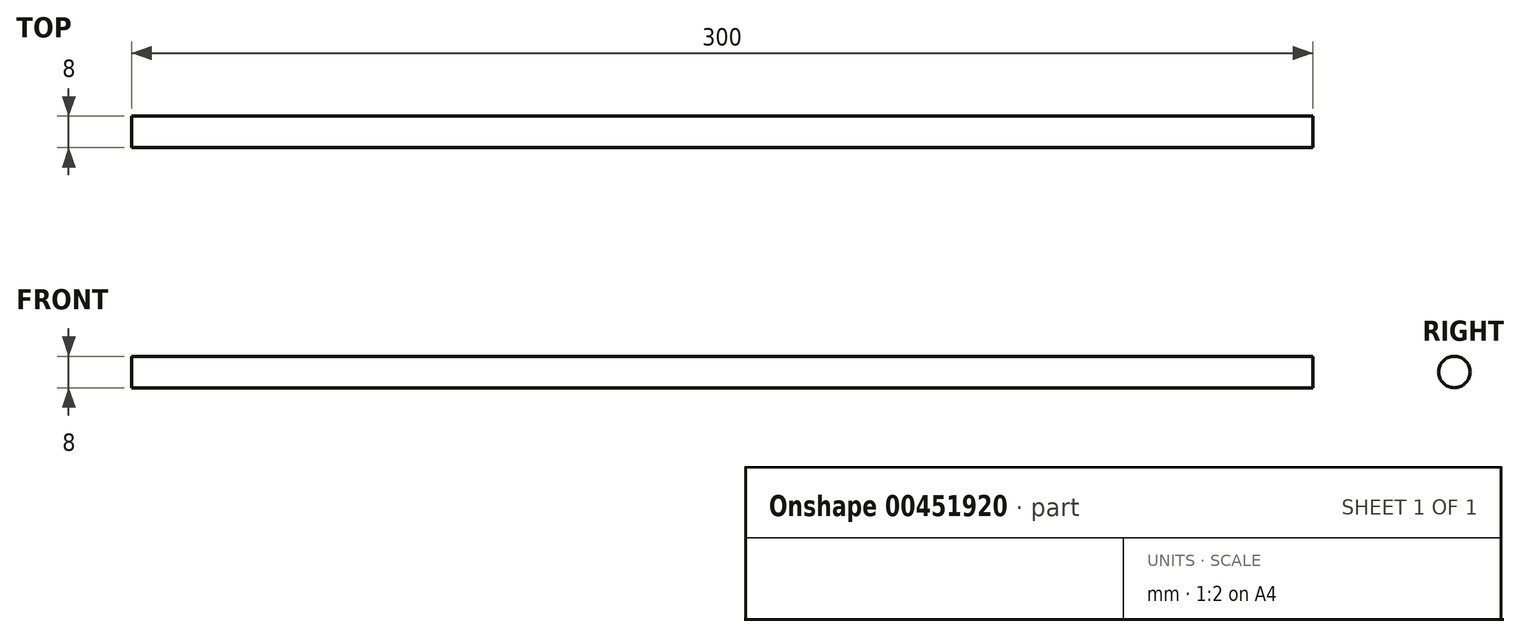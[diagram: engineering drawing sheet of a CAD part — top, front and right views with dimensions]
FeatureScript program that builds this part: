
annotation { "Feature Type Name" : "Feature", "Feature Type Description" : "" }
export const myFeature = defineFeature(function(context is Context, id is Id, definition is map)
    precondition{}
    {
        {
            var Q0;
            Q0=qCreatedBy(makeId("Top.planeOp"),FACE);
            var sketch = newSketch(context, id + "F0", { "sketchPlane" : qUnion([Q0])});
            skLineSegment(sketch, "E0", {"start": v(-150, 0) * mm, "end": v(-150, 4) * mm});
            skLineSegment(sketch, "E1", {"start": v(-150, 4) * mm, "end": v(-50, 4) * mm});
            skLineSegment(sketch, "E2", {"start": v(-50, 4) * mm, "end": v(-50, 4) * mm});
            skLineSegment(sketch, "E3", {"start": v(-50, 4) * mm, "end": v(0, 4) * mm});
            skLineSegment(sketch, "E4", {"start": v(0, -10.3) * mm, "end": v(0, 18.1) * mm, "construction": true});
            skLineSegment(sketch, "E5", {"start": v(-54.75, 0) * mm, "end": v(22.4, 0) * mm, "construction": true});
            skLineSegment(sketch, "E6.MirrorCS", {"start": v(150, 0) * mm, "end": v(150, 4) * mm});
            skLineSegment(sketch, "E7.MirrorCS", {"start": v(50, 4) * mm, "end": v(50, 4) * mm});
            skLineSegment(sketch, "E8.MirrorCS", {"start": v(150, 4) * mm, "end": v(50, 4) * mm});
            skLineSegment(sketch, "E9.MirrorCS", {"start": v(50, 4) * mm, "end": v(0, 4) * mm});
            skLineSegment(sketch, "E10", {"start": v(-150, 0) * mm, "end": v(150, 0) * mm});
            skSolve(sketch);
        }
        {
            var Q0;
            Q0=makeQuery(id+"F0.imprint","IMPRINT",FACE,{"disambiguationData":[TD([[makeQuery(id+"F0.imprint","IMPRINT",EDGE,{"derivedFrom":sQuery(id+"F0.wireOp",EDGE,"E0")}),-1.0]])]});
            var Q1;
            Q1=sQuery(id+"F0.wireOp",EDGE,"E10");
            revolve(context, id + "F1", {"entities" : qUnion([Q0]), "axis" : qUnion([Q1]), "revolveType" : RevolveType.FULL});
        }
    });
